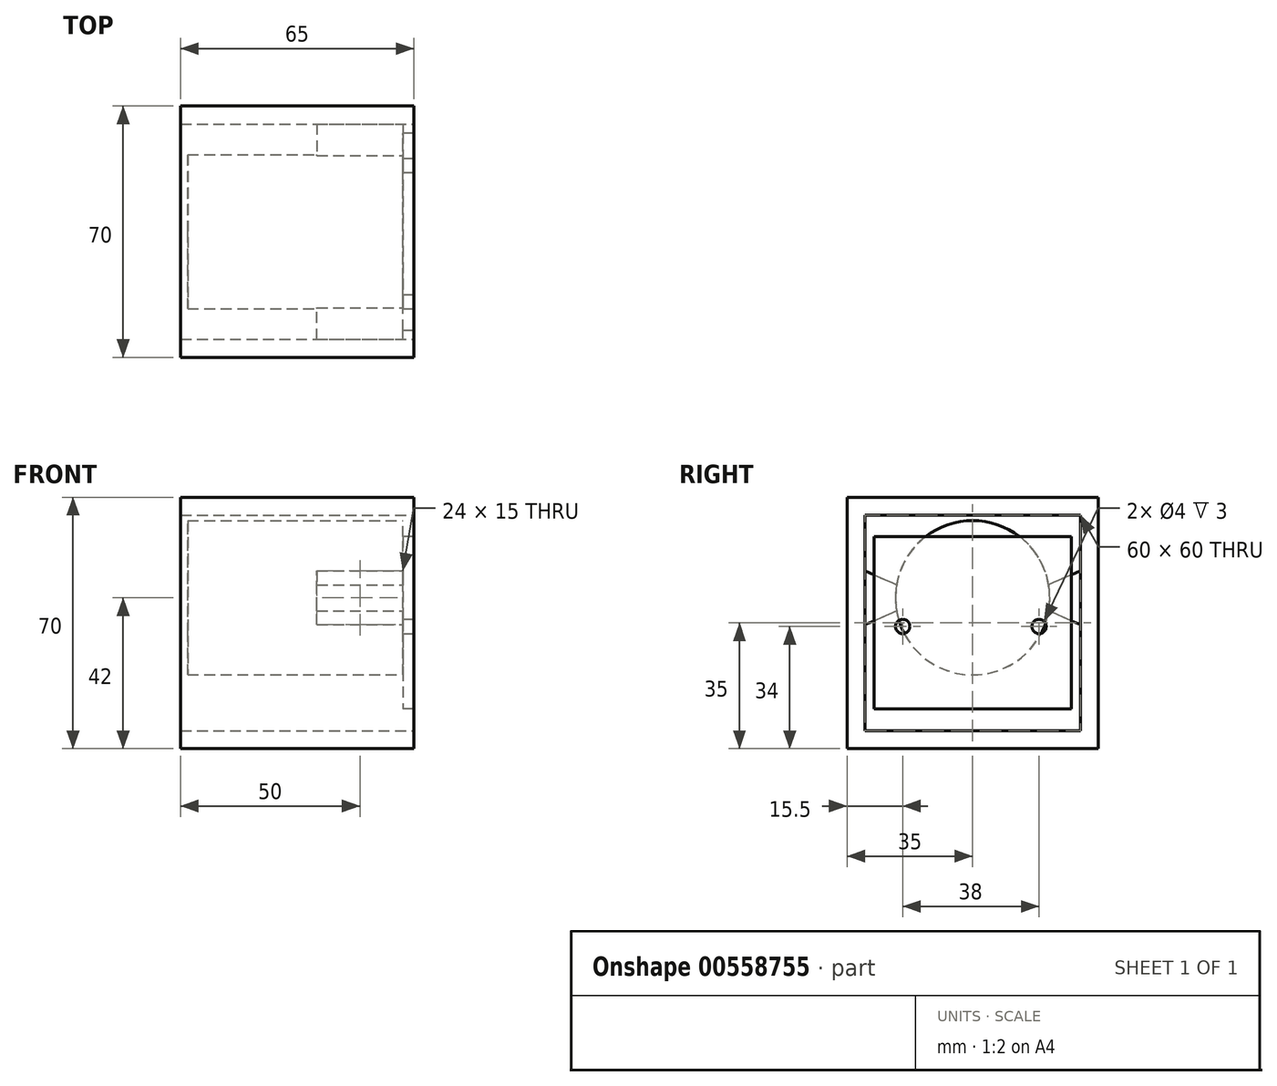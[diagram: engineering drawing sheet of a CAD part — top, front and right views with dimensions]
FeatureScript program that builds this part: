
annotation { "Feature Type Name" : "Feature", "Feature Type Description" : "" }
export const myFeature = defineFeature(function(context is Context, id is Id, definition is map)
    precondition{}
    {
        {
            var Q0;
            Q0=qCreatedBy(makeId("Right.planeOp"),FACE);
            var sketch = newSketch(context, id + "F0", { "sketchPlane" : qUnion([Q0])});
            skLineSegment(sketch, "E0.bottom", {"start": v(-27.5, 24) * mm, "end": v(27.5, 24) * mm});
            skLineSegment(sketch, "E0.top", {"start": v(-27.5, -24) * mm, "end": v(27.5, -24) * mm});
            skLineSegment(sketch, "E0.left", {"start": v(-27.5, 24) * mm, "end": v(-27.5, -24) * mm});
            skLineSegment(sketch, "E0.right", {"start": v(27.5, 24) * mm, "end": v(27.5, -24) * mm});
            skPoint(sketch, "E0.middle", {"position": v(0, 0) * mm});
            skSolve(sketch);
        }
        {
            var Q0;
            Q0=makeQuery(id+"F0.imprint","IMPRINT",FACE,{"disambiguationData":[TD([[makeQuery(id+"F0.imprint","IMPRINT",EDGE,{"derivedFrom":sQuery(id+"F0.wireOp",EDGE,"E0.bottom")}),-1.0]])]});
            extrude(context, id + "F1", {"entities" : qUnion([Q0]), "depth" : 3 * mm, "offsetDistance" : 25 * mm});
        }
        {
            var Q0;
            Q0=makeQuery(id+"F1.opExtrude","CAP_FACE",FACE,{"disambiguationData":[OSD([sQuery(id+"F0.wireOp",EDGE,"E0.bottom"),sQuery(id+"F0.wireOp",EDGE,"E0.top"),sQuery(id+"F0.wireOp",EDGE,"E0.left"),sQuery(id+"F0.wireOp",EDGE,"E0.right")])],"isStart":true});
            var sketch = newSketch(context, id + "F2", { "sketchPlane" : qUnion([Q0])});
            skCircle(sketch, "E1", {"center": v(-22.9, 7) * mm, "radius": 4 * mm});
            skCircle(sketch, "E2", {"center": v(22.9, 7) * mm, "radius": 4 * mm});
            skSolve(sketch);
        }
        {
            var Q0;
            Q0=makeQuery(id+"F2.imprint","IMPRINT",FACE,{"disambiguationData":[TD([[makeQuery(id+"F2.imprint","IMPRINT",EDGE,{"derivedFrom":sQuery(id+"F2.wireOp",EDGE,"E1")}),1.0]])]});
            var Q1;
            Q1=makeQuery(id+"F2.imprint","IMPRINT",FACE,{"disambiguationData":[TD([[makeQuery(id+"F2.imprint","IMPRINT",EDGE,{"derivedFrom":sQuery(id+"F2.wireOp",EDGE,"E2")}),1.0]])]});
            extrude(context, id + "F3", {"entities" : qUnion([Q0, Q1]), "operationType" : NewBodyOperationType.ADD, "depth" : 23.8 * mm, "offsetDistance" : 25 * mm});
        }
        {
            var Q0;
            Q0=makeQuery(id+"F1.opExtrude","CAP_FACE",FACE,{"disambiguationData":[OSD([sQuery(id+"F0.wireOp",EDGE,"E0.bottom"),sQuery(id+"F0.wireOp",EDGE,"E0.top"),sQuery(id+"F0.wireOp",EDGE,"E0.left"),sQuery(id+"F0.wireOp",EDGE,"E0.right")])],"isStart":false});
            var sketch = newSketch(context, id + "F4", { "sketchPlane" : qUnion([Q0])});
            skCircle(sketch, "E3", {"center": v(-19.5, -1) * mm, "radius": 2 * mm});
            skCircle(sketch, "E4", {"center": v(18.5, -1) * mm, "radius": 2 * mm});
            skSolve(sketch);
        }
        {
            var Q0;
            Q0=makeQuery(id+"F4.imprint","IMPRINT",FACE,{"disambiguationData":[TD([[makeQuery(id+"F4.imprint","IMPRINT",EDGE,{"derivedFrom":sQuery(id+"F4.wireOp",EDGE,"E3")}),1.0]])]});
            var Q1;
            Q1=makeQuery(id+"F4.imprint","IMPRINT",FACE,{"disambiguationData":[TD([[makeQuery(id+"F4.imprint","IMPRINT",EDGE,{"derivedFrom":sQuery(id+"F4.wireOp",EDGE,"E4")}),1.0]])]});
            extrude(context, id + "F5", {"entities" : qUnion([Q0, Q1]), "operationType" : NewBodyOperationType.REMOVE, "oppositeDirection" : true, "depth" : 25 * mm, "offsetDistance" : 25 * mm});
        }
        {
            var Q0;
            Q0=makeQuery(id+"F1.opExtrude","CAP_FACE",FACE,{"disambiguationData":[OSD([sQuery(id+"F0.wireOp",EDGE,"E0.bottom"),sQuery(id+"F0.wireOp",EDGE,"E0.top"),sQuery(id+"F0.wireOp",EDGE,"E0.left"),sQuery(id+"F0.wireOp",EDGE,"E0.right")])],"isStart":false});
            var sketch = newSketch(context, id + "F6", { "sketchPlane" : qUnion([Q0])});
            skLineSegment(sketch, "E5.bottom", {"start": v(-35, 35) * mm, "end": v(35, 35) * mm});
            skLineSegment(sketch, "E5.top", {"start": v(-35, -35) * mm, "end": v(35, -35) * mm});
            skLineSegment(sketch, "E5.left", {"start": v(-35, 35) * mm, "end": v(-35, -35) * mm});
            skLineSegment(sketch, "E5.right", {"start": v(35, 35) * mm, "end": v(35, -35) * mm});
            skPoint(sketch, "E5.middle", {"position": v(0, 0) * mm});
            skLineSegment(sketch, "E6.bottom", {"start": v(-30, 30) * mm, "end": v(30, 30) * mm});
            skLineSegment(sketch, "E6.top", {"start": v(-30, -30) * mm, "end": v(30, -30) * mm});
            skLineSegment(sketch, "E6.left", {"start": v(-30, 30) * mm, "end": v(-30, -30) * mm});
            skLineSegment(sketch, "E6.right", {"start": v(30, 30) * mm, "end": v(30, -30) * mm});
            skSolve(sketch);
        }
        {
            var Q0;
            Q0=makeQuery(id+"F1.opExtrude","CAP_FACE",FACE,{"disambiguationData":[OSD([sQuery(id+"F0.wireOp",EDGE,"E0.bottom"),sQuery(id+"F0.wireOp",EDGE,"E0.top"),sQuery(id+"F0.wireOp",EDGE,"E0.left"),sQuery(id+"F0.wireOp",EDGE,"E0.right")])],"isStart":true});
            var sketch = newSketch(context, id + "F7", { "sketchPlane" : qUnion([Q0])});
            skCircle(sketch, "E7", {"center": v(0, 7) * mm, "radius": 21.5 * mm});
            skSolve(sketch);
        }
        {
            var Q0;
            Q0 = qSketchRegion(id + "F7", true);
            extrude(context, id + "F8", {"entities" : qUnion([Q0]), "operationType" : NewBodyOperationType.ADD, "depth" : 60 * mm, "offsetDistance" : 25 * mm});
        }
        {
            var Q0;
            Q0=makeQuery(id+"F6.imprint","IMPRINT",FACE,{"disambiguationData":[TD([[makeQuery(id+"F6.imprint","IMPRINT",EDGE,{"derivedFrom":sQuery(id+"F6.wireOp",EDGE,"E5.bottom")}),-1.0]])]});
            extrude(context, id + "F9", {"entities" : qUnion([Q0]), "oppositeDirection" : true, "depth" : 65 * mm, "offsetDistance" : 25 * mm});
        }
        {
            var Q0;
            Q0=qCreatedBy(makeId("Right.planeOp"),FACE);
            var sketch = newSketch(context, id + "F10", { "sketchPlane" : qUnion([Q0])});
            skArc(sketch, "E8", {"start": v(21.29, 10.66) * mm, "mid": v(18.9, 7) * mm, "end": v(21.29, 3.34) * mm});
            skArc(sketch, "E9", {"start": v(-21.29, 3.34) * mm, "mid": v(-18.9, 7) * mm, "end": v(-21.29, 10.66) * mm});
            skLineSegment(sketch, "E10", {"start": v(30, -0.5) * mm, "end": v(30, 14.5) * mm});
            skLineSegment(sketch, "E11", {"start": v(30, 14.5) * mm, "end": v(21.29, 10.66) * mm});
            skLineSegment(sketch, "E12", {"start": v(30, -0.5) * mm, "end": v(21.29, 3.34) * mm});
            skLineSegment(sketch, "E13", {"start": v(-30, 14.5) * mm, "end": v(-30, -0.5) * mm});
            skLineSegment(sketch, "E14", {"start": v(-30, -0.5) * mm, "end": v(-21.29, 3.34) * mm});
            skLineSegment(sketch, "E15", {"start": v(-30, 14.5) * mm, "end": v(-21.29, 10.66) * mm});
            skSolve(sketch);
        }
        {
            var Q0;
            Q0=makeQuery(id+"F10.imprint","IMPRINT",FACE,{"disambiguationData":[TD([[makeQuery(id+"F10.imprint","IMPRINT",EDGE,{"derivedFrom":sQuery(id+"F10.wireOp",EDGE,"E9")}),1.0]])]});
            var Q1;
            Q1=makeQuery(id+"F10.imprint","IMPRINT",FACE,{"disambiguationData":[TD([[makeQuery(id+"F10.imprint","IMPRINT",EDGE,{"derivedFrom":sQuery(id+"F10.wireOp",EDGE,"E8")}),1.0]])]});
            extrude(context, id + "F11", {"entities" : qUnion([Q0, Q1]), "operationType" : NewBodyOperationType.ADD, "oppositeDirection" : true, "depth" : 24 * mm, "offsetDistance" : 25 * mm});
        }
    });
